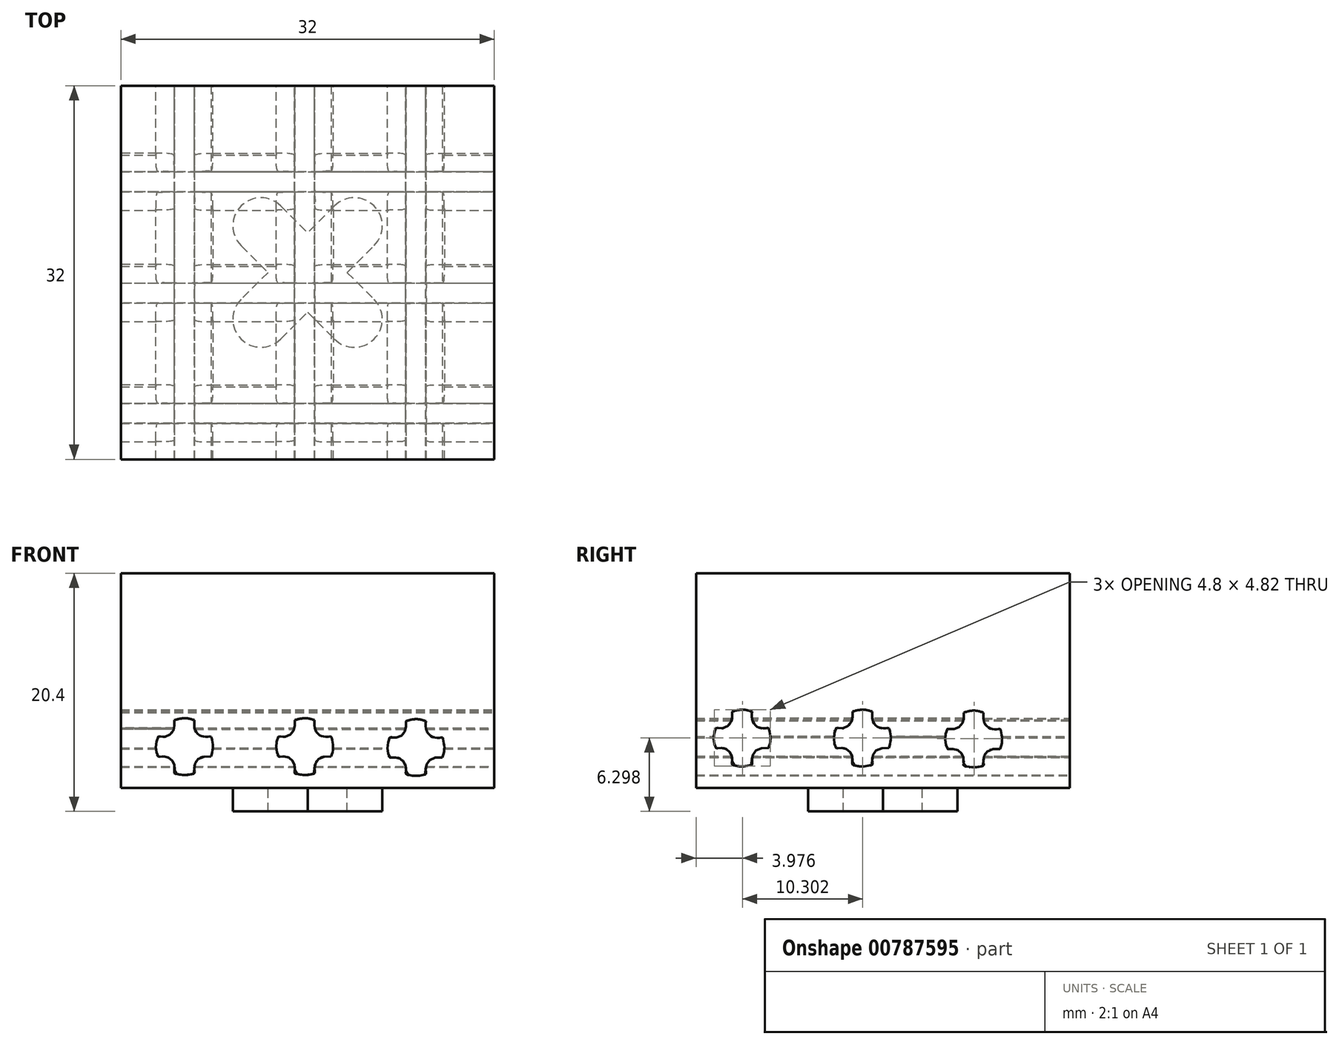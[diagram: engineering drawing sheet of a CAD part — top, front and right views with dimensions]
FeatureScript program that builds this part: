
annotation { "Feature Type Name" : "Feature", "Feature Type Description" : "" }
export const myFeature = defineFeature(function(context is Context, id is Id, definition is map)
    precondition{}
    {
        {
            var Q0;
            Q0=qCreatedBy(makeId("Top.planeOp"),FACE);
            var sketch = newSketch(context, id + "F0", { "sketchPlane" : qUnion([Q0])});
            skArc(sketch, "E0", {"start": v(-2.3, 5.7) * mm, "mid": v(-5.7, 5.7) * mm, "end": v(-5.7, 2.3) * mm});
            skArc(sketch, "E1", {"start": v(5.7, 2.3) * mm, "mid": v(5.7, 5.7) * mm, "end": v(2.3, 5.7) * mm});
            skArc(sketch, "E2", {"start": v(-5.7, -2.3) * mm, "mid": v(-5.7, -5.7) * mm, "end": v(-2.3, -5.7) * mm});
            skArc(sketch, "E3", {"start": v(2.3, -5.7) * mm, "mid": v(5.7, -5.7) * mm, "end": v(5.7, -2.3) * mm});
            skLineSegment(sketch, "E4", {"start": v(-4, 4) * mm, "end": v(4, -4) * mm, "construction": true});
            skLineSegment(sketch, "E5", {"start": v(-4, -4) * mm, "end": v(4, 4) * mm, "construction": true});
            skPoint(sketch, "E6", {"position": v(0, 0) * mm});
            skLineSegment(sketch, "E7", {"start": v(-5.7, 2.3) * mm, "end": v(-3.4, 0) * mm});
            skLineSegment(sketch, "E8", {"start": v(-2.3, 5.7) * mm, "end": v(0, 3.4) * mm});
            skLineSegment(sketch, "E9", {"start": v(2.3, 5.7) * mm, "end": v(0, 3.4) * mm});
            skLineSegment(sketch, "E10", {"start": v(-2.3, -5.7) * mm, "end": v(0, -3.4) * mm});
            skLineSegment(sketch, "E11.trimOffspring", {"start": v(-3.4, 0) * mm, "end": v(-5.7, -2.3) * mm});
            skLineSegment(sketch, "E12.trimOffspring", {"start": v(3.4, 0) * mm, "end": v(5.7, -2.3) * mm});
            skLineSegment(sketch, "E13.trimOffspring", {"start": v(3.4, 0) * mm, "end": v(5.7, 2.3) * mm});
            skLineSegment(sketch, "E14.trimOffspring", {"start": v(0, -3.4) * mm, "end": v(2.3, -5.7) * mm});
            skSolve(sketch);
        }
        {
            var Q0;
            Q0=qCreatedBy(makeId("Top.planeOp"),FACE);
            var sketch = newSketch(context, id + "F1", { "sketchPlane" : qUnion([Q0])});
            skLineSegment(sketch, "E15.bottom", {"start": v(-16, 16) * mm, "end": v(16, 16) * mm});
            skLineSegment(sketch, "E15.top", {"start": v(-16, -16) * mm, "end": v(16, -16) * mm});
            skLineSegment(sketch, "E15.left", {"start": v(-16, 16) * mm, "end": v(-16, -16) * mm});
            skLineSegment(sketch, "E15.right", {"start": v(16, 16) * mm, "end": v(16, -16) * mm});
            skPoint(sketch, "E16", {"position": v(0, 16) * mm});
            skPoint(sketch, "E17", {"position": v(0, -19) * mm});
            skPoint(sketch, "E18", {"position": v(-16, 0) * mm});
            skArc(sketch, "E19", {"start": v(0, 37.14) * mm, "mid": v(-22.18, 26.57) * mm, "end": v(-26.46, 2.38) * mm});
            skArc(sketch, "E20", {"start": v(-27.14, -4.28) * mm, "mid": v(-26.12, -1.02) * mm, "end": v(-26.46, 2.38) * mm});
            skArc(sketch, "E21.trimOffspring", {"start": v(-27.14, -4.28) * mm, "mid": v(-25.58, -31.95) * mm, "end": v(0, -42.63) * mm});
            skLineSegment(sketch, "E22", {"start": v(0, 72.2) * mm, "end": v(0, -78) * mm});
            skLineSegment(sketch, "E23", {"start": v(0, 37.14) * mm, "end": v(0, -42.63) * mm});
            skSolve(sketch);
        }
        {
            var Q0;
            Q0=qCreatedBy(makeId("Top.planeOp"),FACE);
            var sketch = newSketch(context, id + "F2", { "sketchPlane" : qUnion([Q0])});
            skLineSegment(sketch, "E24.bottom", {"start": v(-16, 16) * mm, "end": v(16, 16) * mm});
            skLineSegment(sketch, "E24.top", {"start": v(-16, -16) * mm, "end": v(16, -16) * mm});
            skLineSegment(sketch, "E24.left", {"start": v(-16, 16) * mm, "end": v(-16, -16) * mm});
            skLineSegment(sketch, "E24.right", {"start": v(16, 16) * mm, "end": v(16, -16) * mm});
            skSolve(sketch);
        }
        {
            var Q0;
            {var subQ1=sQuery(id+"F1.wireOp",EDGE,"E15.left");Q0=makeQuery(id+"F1.imprint","IMPRINT",FACE,{"disambiguationData":[TD([[makeQuery(id+"F1.imprint","IMPRINT",EDGE,{"derivedFrom":subQ1}),-1.0]])]});}
            var Q1;
            Q1=sQuery(id+"F1.wireOp",EDGE,"E22");
            revolve(context, id + "F3", {"surfaceOperationType" : NewSurfaceOperationType.NEW, "entities" : qUnion([Q0]), "axis" : qUnion([Q1]), "revolveType" : RevolveType.FULL});
        }
        {
            var Q0;
            Q0 = qSketchRegion(id + "F2", true);
            extrude(context, id + "F4", {"entities" : qUnion([Q0]), "operationType" : NewBodyOperationType.REMOVE, "endBound" : BoundingType.THROUGH_ALL, "oppositeDirection" : true, "depth" : 166.3 * mm, "offsetDistance" : 25 * mm});
        }
        {
            var Q0;
            Q0=makeQuery(id+"F4.boolean.opBoolean","INTERSECT",EDGE,{"derivedFrom":[makeQuery(id+"F3.opRevolve","SWEPT_FACE",FACE,{"disambiguationData":[OSD([sQuery(id+"F1.wireOp",EDGE,"E20")])]}),makeQuery(id+"F4.opExtrude","SWEPT_FACE",FACE,{"disambiguationData":[OSD([sQuery(id+"F2.wireOp",EDGE,"E24.right")])]})]});
            var Q1;
            Q1=makeQuery(id+"F4.boolean.opBoolean","INTERSECT",EDGE,{"derivedFrom":[makeQuery(id+"F3.opRevolve","SWEPT_FACE",FACE,{"disambiguationData":[OSD([sQuery(id+"F1.wireOp",EDGE,"E19")])]}),makeQuery(id+"F4.opExtrude","SWEPT_FACE",FACE,{"disambiguationData":[OSD([sQuery(id+"F2.wireOp",EDGE,"E24.right")])]})]});
            var Q2;
            Q2=makeQuery(id+"F4.boolean.opBoolean","INTERSECT",EDGE,{"derivedFrom":[makeQuery(id+"F3.opRevolve","SWEPT_FACE",FACE,{"disambiguationData":[OSD([sQuery(id+"F1.wireOp",EDGE,"E19")])]}),makeQuery(id+"F4.opExtrude","SWEPT_FACE",FACE,{"disambiguationData":[OSD([sQuery(id+"F2.wireOp",EDGE,"E24.bottom")])]})]});
            var Q3;
            Q3=makeQuery(id+"F4.boolean.opBoolean","INTERSECT",EDGE,{"derivedFrom":[makeQuery(id+"F3.opRevolve","SWEPT_FACE",FACE,{"disambiguationData":[OSD([sQuery(id+"F1.wireOp",EDGE,"E19")])]}),makeQuery(id+"F4.opExtrude","SWEPT_FACE",FACE,{"disambiguationData":[OSD([sQuery(id+"F2.wireOp",EDGE,"E24.left")])]})]});
            var Q4;
            Q4=makeQuery(id+"F4.boolean.opBoolean","INTERSECT",EDGE,{"derivedFrom":[makeQuery(id+"F3.opRevolve","SWEPT_FACE",FACE,{"disambiguationData":[OSD([sQuery(id+"F1.wireOp",EDGE,"E20")])]}),makeQuery(id+"F4.opExtrude","SWEPT_FACE",FACE,{"disambiguationData":[OSD([sQuery(id+"F2.wireOp",EDGE,"E24.top")])]})]});
            var Q5;
            Q5=makeQuery(id+"F4.boolean.opBoolean","INTERSECT",EDGE,{"derivedFrom":[makeQuery(id+"F3.opRevolve","SWEPT_FACE",FACE,{"disambiguationData":[OSD([sQuery(id+"F1.wireOp",EDGE,"E21.trimOffspring")])]}),makeQuery(id+"F4.opExtrude","SWEPT_FACE",FACE,{"disambiguationData":[OSD([sQuery(id+"F2.wireOp",EDGE,"E24.right")])]})]});
            var Q6;
            Q6=makeQuery(id+"F4.boolean.opBoolean","INTERSECT",EDGE,{"derivedFrom":[makeQuery(id+"F3.opRevolve","SWEPT_FACE",FACE,{"disambiguationData":[OSD([sQuery(id+"F1.wireOp",EDGE,"E21.trimOffspring")])]}),makeQuery(id+"F4.opExtrude","SWEPT_FACE",FACE,{"disambiguationData":[OSD([sQuery(id+"F2.wireOp",EDGE,"E24.left")])]})]});
            fillet(context, id + "F5", {"entities" : qUnion([Q0, Q1, Q2, Q3, Q4, Q5, Q6]), "radius" : 4 * mm, "tangentPropagation" : true, "allowEdgeOverflow" : false});
        }
        {
            var Q0;
            Q0=makeQuery(id+"F2.imprint","IMPRINT",FACE,{"disambiguationData":[TD([[makeQuery(id+"F2.imprint","IMPRINT",EDGE,{"derivedFrom":sQuery(id+"F2.wireOp",EDGE,"E24.bottom")}),-1.0]])]});
            extrude(context, id + "F6", {"entities" : qUnion([Q0]), "depth" : 18.4 * mm, "offsetDistance" : 25 * mm});
        }
        {
            var Q0;
            Q0=makeQuery(id+"F0.imprint","IMPRINT",FACE,{"disambiguationData":[TD([[makeQuery(id+"F0.imprint","IMPRINT",EDGE,{"derivedFrom":sQuery(id+"F0.wireOp",EDGE,"E0")}),1.0]])]});
            extrude(context, id + "F7", {"entities" : qUnion([Q0]), "oppositeDirection" : true, "depth" : 2 * mm, "offsetDistance" : 25 * mm});
        }
        {
            var Q0;
            Q0=qCreatedBy(makeId("Right.planeOp"),FACE);
            var sketch = newSketch(context, id + "F8", { "sketchPlane" : qUnion([Q0])});
            skFitSpline(sketch, "E25", {"points": [v(-12.91, 6.54) * mm, v(-12.03, 6.7) * mm, v(-11.21, 6.54) * mm], "startDerivative": vector(1.75, 0.5) * mm, "endDerivative": vector(1.65, -0.5) * mm});
            skFitSpline(sketch, "E26", {"points": [v(-11.21, 6.54) * mm, v(-11.2, 5.98) * mm, v(-11.06, 5.54) * mm, v(-10.75, 5.24) * mm, v(-10.4, 5.13) * mm, v(-9.99, 5.12) * mm, v(-9.79, 5.12) * mm, v(-9.7, 4.88) * mm, v(-9.63, 4.5) * mm, v(-9.63, 4.15) * mm, v(-9.67, 3.83) * mm, v(-9.79, 3.42) * mm], "startDerivative": vector(-0.26, -5.18) * mm, "endDerivative": vector(-1.41, -4.37) * mm});
            skFitSpline(sketch, "E27", {"points": [v(-12.91, 6.54) * mm, v(-12.91, 6.25) * mm, v(-12.91, 6) * mm, v(-12.94, 5.81) * mm, v(-13.11, 5.47) * mm, v(-13.31, 5.29) * mm, v(-13.57, 5.16) * mm, v(-13.89, 5.12) * mm, v(-14.33, 5.12) * mm, v(-14.42, 4.84) * mm, v(-14.48, 4.55) * mm, v(-14.5, 4.23) * mm, v(-14.47, 3.94) * mm, v(-14.41, 3.67) * mm, v(-14.33, 3.42) * mm, v(-14.14, 3.42) * mm, v(-13.82, 3.42) * mm, v(-13.57, 3.38) * mm, v(-13.39, 3.3) * mm, v(-13.16, 3.13) * mm, v(-13.05, 3) * mm, v(-12.97, 2.81) * mm, v(-12.91, 2.56) * mm, v(-12.91, 2.32) * mm, v(-12.91, 2) * mm, v(-12.65, 1.92) * mm, v(-12.3, 1.86) * mm, v(-12.03, 1.85) * mm, v(-11.76, 1.86) * mm, v(-11.4, 1.94) * mm, v(-11.21, 2) * mm, v(-11.21, 2.32) * mm, v(-11.2, 2.6) * mm, v(-11.1, 2.92) * mm, v(-10.97, 3.12) * mm, v(-10.7, 3.32) * mm, v(-10.29, 3.42) * mm, v(-9.79, 3.42) * mm], "startDerivative": vector(-0.02, -10.87) * mm, "endDerivative": vector(14.17, -0.52) * mm});
            skFitSpline(sketch, "E28", {"points": [v(-2.6, 6.54) * mm, v(-1.72, 6.7) * mm, v(-0.9, 6.54) * mm], "startDerivative": vector(1.75, 0.5) * mm, "endDerivative": vector(1.65, -0.5) * mm});
            skFitSpline(sketch, "E29", {"points": [v(-0.9, 6.54) * mm, v(-0.9, 5.98) * mm, v(-0.76, 5.54) * mm, v(-0.44, 5.24) * mm, v(-0.1, 5.13) * mm, v(0.31, 5.12) * mm, v(0.51, 5.12) * mm, v(0.6, 4.88) * mm, v(0.67, 4.5) * mm, v(0.68, 4.15) * mm, v(0.63, 3.83) * mm, v(0.51, 3.42) * mm], "startDerivative": vector(-0.26, -5.18) * mm, "endDerivative": vector(-1.41, -4.37) * mm});
            skFitSpline(sketch, "E30", {"points": [v(-2.6, 6.54) * mm, v(-2.6, 6.25) * mm, v(-2.6, 6) * mm, v(-2.64, 5.81) * mm, v(-2.8, 5.47) * mm, v(-3, 5.29) * mm, v(-3.27, 5.16) * mm, v(-3.59, 5.12) * mm, v(-4.03, 5.12) * mm, v(-4.12, 4.84) * mm, v(-4.18, 4.55) * mm, v(-4.2, 4.23) * mm, v(-4.17, 3.94) * mm, v(-4.1, 3.67) * mm, v(-4.03, 3.42) * mm, v(-3.83, 3.42) * mm, v(-3.52, 3.42) * mm, v(-3.27, 3.38) * mm, v(-3.08, 3.3) * mm, v(-2.86, 3.13) * mm, v(-2.75, 3) * mm, v(-2.66, 2.81) * mm, v(-2.61, 2.56) * mm, v(-2.6, 2.32) * mm, v(-2.6, 2) * mm, v(-2.35, 1.92) * mm, v(-2, 1.86) * mm, v(-1.72, 1.85) * mm, v(-1.46, 1.86) * mm, v(-1.1, 1.94) * mm, v(-0.9, 2) * mm, v(-0.9, 2.32) * mm, v(-0.9, 2.6) * mm, v(-0.8, 2.92) * mm, v(-0.67, 3.12) * mm, v(-0.4, 3.32) * mm, v(0.02, 3.42) * mm, v(0.51, 3.42) * mm], "startDerivative": vector(-0.02, -10.87) * mm, "endDerivative": vector(14.17, -0.52) * mm});
            skFitSpline(sketch, "E31", {"points": [v(6.92, 6.46) * mm, v(7.8, 6.63) * mm, v(8.62, 6.46) * mm], "startDerivative": vector(1.75, 0.5) * mm, "endDerivative": vector(1.65, -0.5) * mm});
            skFitSpline(sketch, "E32", {"points": [v(8.62, 6.46) * mm, v(8.63, 5.9) * mm, v(8.77, 5.46) * mm, v(9.09, 5.17) * mm, v(9.43, 5.05) * mm, v(9.84, 5.04) * mm, v(10.04, 5.04) * mm, v(10.12, 4.8) * mm, v(10.2, 4.41) * mm, v(10.2, 4.07) * mm, v(10.17, 3.76) * mm, v(10.04, 3.34) * mm], "startDerivative": vector(-0.26, -5.18) * mm, "endDerivative": vector(-1.41, -4.37) * mm});
            skFitSpline(sketch, "E33", {"points": [v(6.92, 6.46) * mm, v(6.92, 6.17) * mm, v(6.92, 5.92) * mm, v(6.9, 5.73) * mm, v(6.72, 5.4) * mm, v(6.52, 5.2) * mm, v(6.26, 5.08) * mm, v(5.94, 5.04) * mm, v(5.5, 5.04) * mm, v(5.41, 4.76) * mm, v(5.36, 4.48) * mm, v(5.34, 4.15) * mm, v(5.36, 3.86) * mm, v(5.42, 3.6) * mm, v(5.5, 3.34) * mm, v(5.7, 3.34) * mm, v(6.01, 3.34) * mm, v(6.26, 3.3) * mm, v(6.45, 3.23) * mm, v(6.67, 3.05) * mm, v(6.78, 2.91) * mm, v(6.87, 2.73) * mm, v(6.92, 2.49) * mm, v(6.92, 2.24) * mm, v(6.92, 1.92) * mm, v(7.18, 1.84) * mm, v(7.53, 1.78) * mm, v(7.8, 1.77) * mm, v(8.07, 1.79) * mm, v(8.44, 1.86) * mm, v(8.62, 1.92) * mm, v(8.62, 2.24) * mm, v(8.63, 2.52) * mm, v(8.73, 2.85) * mm, v(8.86, 3.04) * mm, v(9.13, 3.24) * mm, v(9.55, 3.34) * mm, v(10.04, 3.34) * mm], "startDerivative": vector(-0.02, -10.87) * mm, "endDerivative": vector(14.17, -0.52) * mm});
            skSolve(sketch);
        }
        {
            var Q0;
            Q0 = qSketchRegion(id + "F8", true);
            extrude(context, id + "F9", {"entities" : qUnion([Q0]), "operationType" : NewBodyOperationType.REMOVE, "oppositeDirection" : true, "depth" : 72.1 * mm, "offsetDistance" : 25 * mm, "hasSecondDirection" : true, "secondDirectionOppositeDirection" : false, "secondDirectionDepth" : 69.3 * mm});
        }
        {
            var Q0;
            Q0=qCreatedBy(makeId("Front.planeOp"),FACE);
            var sketch = newSketch(context, id + "F10", { "sketchPlane" : qUnion([Q0])});
            skFitSpline(sketch, "E34", {"points": [v(-11.4, 5.81) * mm, v(-10.52, 5.98) * mm, v(-9.7, 5.81) * mm], "startDerivative": vector(1.75, 0.5) * mm, "endDerivative": vector(1.65, -0.5) * mm});
            skFitSpline(sketch, "E35", {"points": [v(-9.7, 5.81) * mm, v(-9.7, 5.25) * mm, v(-9.55, 4.81) * mm, v(-9.24, 4.51) * mm, v(-8.9, 4.4) * mm, v(-8.48, 4.4) * mm, v(-8.28, 4.4) * mm, v(-8.2, 4.15) * mm, v(-8.13, 3.76) * mm, v(-8.12, 3.42) * mm, v(-8.16, 3.1) * mm, v(-8.28, 2.7) * mm], "startDerivative": vector(-0.26, -5.18) * mm, "endDerivative": vector(-1.41, -4.37) * mm});
            skFitSpline(sketch, "E36", {"points": [v(-11.4, 5.81) * mm, v(-11.4, 5.52) * mm, v(-11.4, 5.27) * mm, v(-11.43, 5.08) * mm, v(-11.6, 4.74) * mm, v(-11.8, 4.55) * mm, v(-12.06, 4.43) * mm, v(-12.38, 4.4) * mm, v(-12.82, 4.4) * mm, v(-12.91, 4.11) * mm, v(-12.97, 3.82) * mm, v(-13, 3.5) * mm, v(-12.96, 3.2) * mm, v(-12.9, 2.94) * mm, v(-12.82, 2.7) * mm, v(-12.63, 2.7) * mm, v(-12.31, 2.7) * mm, v(-12.07, 2.65) * mm, v(-11.88, 2.57) * mm, v(-11.65, 2.4) * mm, v(-11.55, 2.26) * mm, v(-11.46, 2.08) * mm, v(-11.4, 1.83) * mm, v(-11.4, 1.59) * mm, v(-11.4, 1.27) * mm, v(-11.15, 1.2) * mm, v(-10.8, 1.13) * mm, v(-10.52, 1.12) * mm, v(-10.25, 1.13) * mm, v(-9.89, 1.2) * mm, v(-9.7, 1.27) * mm, v(-9.7, 1.59) * mm, v(-9.7, 1.86) * mm, v(-9.6, 2.2) * mm, v(-9.46, 2.39) * mm, v(-9.2, 2.6) * mm, v(-8.78, 2.7) * mm, v(-8.28, 2.7) * mm], "startDerivative": vector(-0.02, -10.87) * mm, "endDerivative": vector(14.17, -0.52) * mm});
            skFitSpline(sketch, "E37", {"points": [v(-1.1, 5.81) * mm, v(-0.22, 5.98) * mm, v(0.6, 5.81) * mm], "startDerivative": vector(1.75, 0.5) * mm, "endDerivative": vector(1.65, -0.5) * mm});
            skFitSpline(sketch, "E38", {"points": [v(0.6, 5.81) * mm, v(0.6, 5.25) * mm, v(0.75, 4.81) * mm, v(1.06, 4.51) * mm, v(1.4, 4.4) * mm, v(1.82, 4.4) * mm, v(2.02, 4.4) * mm, v(2.1, 4.15) * mm, v(2.18, 3.76) * mm, v(2.19, 3.42) * mm, v(2.14, 3.1) * mm, v(2.02, 2.7) * mm], "startDerivative": vector(-0.26, -5.18) * mm, "endDerivative": vector(-1.41, -4.37) * mm});
            skFitSpline(sketch, "E39", {"points": [v(-1.1, 5.81) * mm, v(-1.1, 5.52) * mm, v(-1.1, 5.27) * mm, v(-1.13, 5.08) * mm, v(-1.3, 4.74) * mm, v(-1.5, 4.55) * mm, v(-1.76, 4.43) * mm, v(-2.08, 4.4) * mm, v(-2.52, 4.4) * mm, v(-2.61, 4.11) * mm, v(-2.67, 3.82) * mm, v(-2.69, 3.5) * mm, v(-2.66, 3.2) * mm, v(-2.6, 2.94) * mm, v(-2.52, 2.7) * mm, v(-2.33, 2.7) * mm, v(-2.01, 2.7) * mm, v(-1.76, 2.65) * mm, v(-1.57, 2.57) * mm, v(-1.35, 2.4) * mm, v(-1.24, 2.26) * mm, v(-1.16, 2.08) * mm, v(-1.1, 1.83) * mm, v(-1.1, 1.59) * mm, v(-1.1, 1.27) * mm, v(-0.84, 1.2) * mm, v(-0.5, 1.13) * mm, v(-0.22, 1.12) * mm, v(0.05, 1.13) * mm, v(0.42, 1.2) * mm, v(0.6, 1.27) * mm, v(0.6, 1.59) * mm, v(0.6, 1.86) * mm, v(0.7, 2.2) * mm, v(0.84, 2.39) * mm, v(1.1, 2.6) * mm, v(1.52, 2.7) * mm, v(2.02, 2.7) * mm], "startDerivative": vector(-0.02, -10.87) * mm, "endDerivative": vector(14.17, -0.52) * mm});
            skFitSpline(sketch, "E40", {"points": [v(8.43, 5.73) * mm, v(9.31, 5.9) * mm, v(10.13, 5.73) * mm], "startDerivative": vector(1.75, 0.5) * mm, "endDerivative": vector(1.65, -0.5) * mm});
            skFitSpline(sketch, "E41", {"points": [v(10.13, 5.73) * mm, v(10.13, 5.17) * mm, v(10.28, 4.73) * mm, v(10.6, 4.43) * mm, v(10.94, 4.32) * mm, v(11.35, 4.31) * mm, v(11.55, 4.31) * mm, v(11.63, 4.07) * mm, v(11.7, 3.68) * mm, v(11.72, 3.34) * mm, v(11.67, 3.03) * mm, v(11.55, 2.61) * mm], "startDerivative": vector(-0.26, -5.18) * mm, "endDerivative": vector(-1.41, -4.37) * mm});
            skFitSpline(sketch, "E42", {"points": [v(8.43, 5.73) * mm, v(8.43, 5.44) * mm, v(8.43, 5.2) * mm, v(8.4, 5) * mm, v(8.23, 4.66) * mm, v(8.03, 4.48) * mm, v(7.77, 4.35) * mm, v(7.45, 4.31) * mm, v(7, 4.31) * mm, v(6.92, 4.03) * mm, v(6.86, 3.74) * mm, v(6.84, 3.42) * mm, v(6.87, 3.13) * mm, v(6.93, 2.86) * mm, v(7, 2.61) * mm, v(7.2, 2.61) * mm, v(7.52, 2.61) * mm, v(7.77, 2.57) * mm, v(7.96, 2.5) * mm, v(8.18, 2.32) * mm, v(8.29, 2.18) * mm, v(8.38, 2) * mm, v(8.43, 1.75) * mm, v(8.43, 1.5) * mm, v(8.43, 1.2) * mm, v(8.69, 1.11) * mm, v(9.04, 1.05) * mm, v(9.31, 1.04) * mm, v(9.58, 1.06) * mm, v(9.95, 1.13) * mm, v(10.13, 1.2) * mm, v(10.13, 1.5) * mm, v(10.14, 1.79) * mm, v(10.24, 2.12) * mm, v(10.37, 2.3) * mm, v(10.64, 2.51) * mm, v(11.06, 2.61) * mm, v(11.55, 2.61) * mm], "startDerivative": vector(-0.02, -10.87) * mm, "endDerivative": vector(14.17, -0.52) * mm});
            skSolve(sketch);
        }
        {
            var Q0;
            Q0 = qSketchRegion(id + "F10", true);
            extrude(context, id + "F11", {"entities" : qUnion([Q0]), "operationType" : NewBodyOperationType.REMOVE, "oppositeDirection" : true, "depth" : 41.6 * mm, "offsetDistance" : 25 * mm, "hasSecondDirection" : true, "secondDirectionOppositeDirection" : false, "secondDirectionDepth" : 47.7 * mm});
        }
    });
